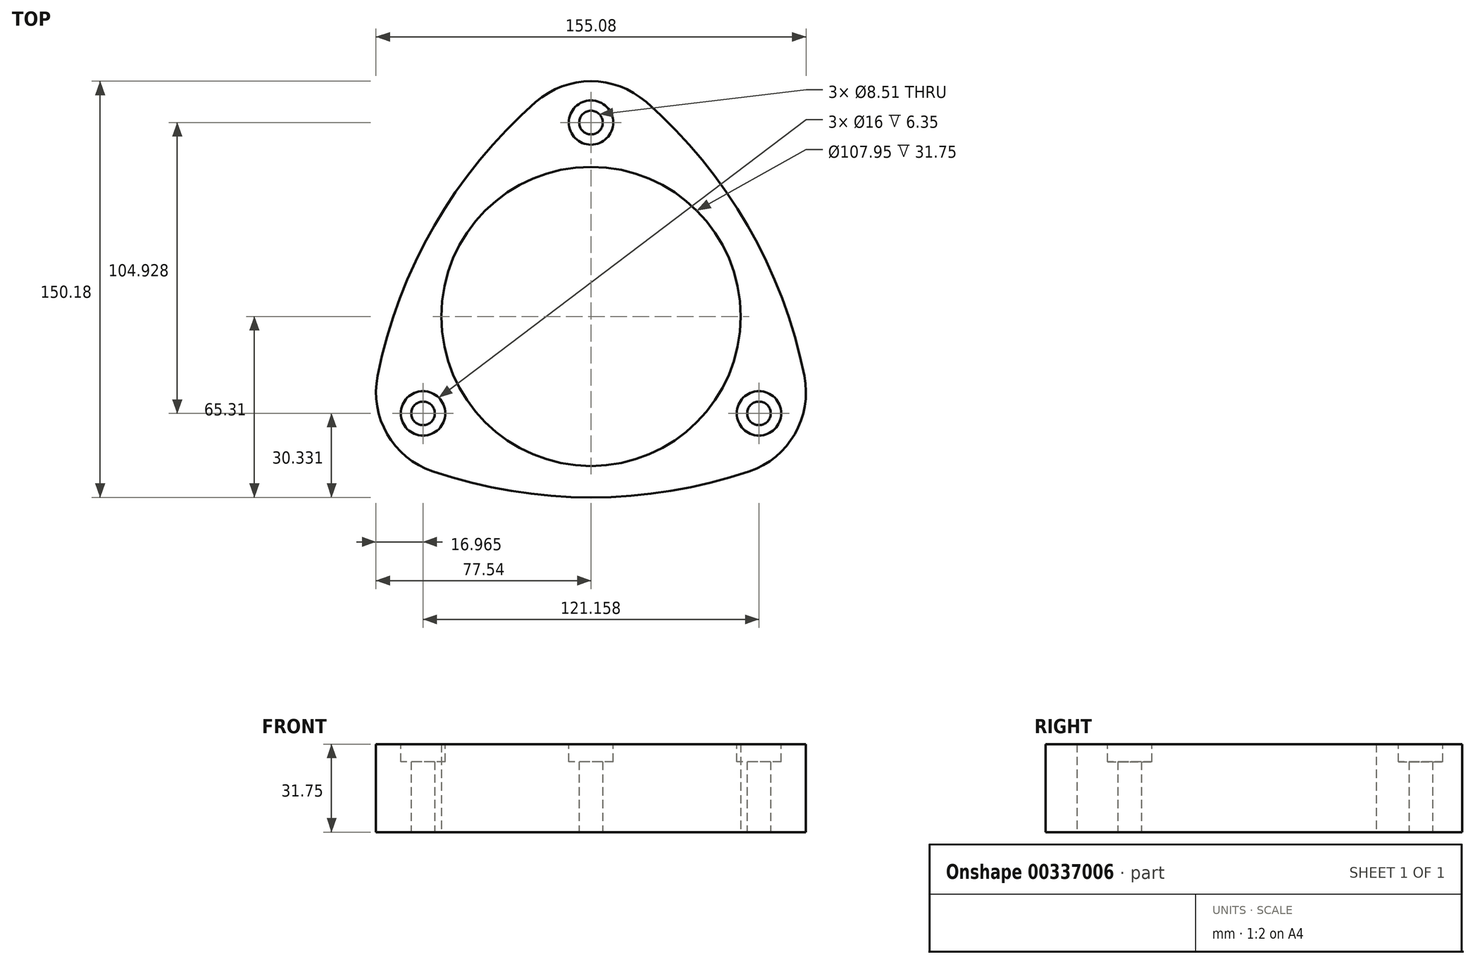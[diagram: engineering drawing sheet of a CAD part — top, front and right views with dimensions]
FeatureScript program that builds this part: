
annotation { "Feature Type Name" : "Feature", "Feature Type Description" : "" }
export const myFeature = defineFeature(function(context is Context, id is Id, definition is map)
    precondition{}
    {
        {
            var Q0;
            Q0=qCreatedBy(makeId("Top.planeOp"),FACE);
            var sketch = newSketch(context, id + "F0", { "sketchPlane" : qUnion([Q0])});
            skCircle(sketch, "E0", {"center": v(0, 0) * mm, "radius": 53.97 * mm});
            skCircle(sketch, "E1", {"center": v(0, 69.95) * mm, "radius": 4.25 * mm});
            skCircle(sketch, "E2", {"center": v(-60.57, -34.98) * mm, "radius": 4.25 * mm});
            skCircle(sketch, "E3", {"center": v(60.58, -34.97) * mm, "radius": 4.25 * mm});
            skArc(sketch, "E4", {"start": v(19.92, 77.36) * mm, "mid": v(0, 84.87) * mm, "end": v(-19.92, 77.36) * mm});
            skLineSegment(sketch, "E5", {"start": v(0, 0) * mm, "end": v(-60.57, -34.98) * mm, "construction": true});
            skLineSegment(sketch, "E6", {"start": v(0, 0) * mm, "end": v(60.58, -34.97) * mm, "construction": true});
            skLineSegment(sketch, "E7", {"start": v(0, 0) * mm, "end": v(0, 69.95) * mm, "construction": true});
            skArc(sketch, "E8", {"start": v(57.04, -55.92) * mm, "mid": v(73.5, -42.43) * mm, "end": v(76.95, -21.43) * mm});
            skArc(sketch, "E9", {"start": v(-76.95, -21.44) * mm, "mid": v(-73.5, -42.44) * mm, "end": v(-57.03, -55.93) * mm});
            skArc(sketch, "E10", {"start": v(-19.92, 77.36) * mm, "mid": v(-56.56, 32.65) * mm, "end": v(-76.95, -21.44) * mm});
            skArc(sketch, "E11", {"start": v(76.95, -21.43) * mm, "mid": v(56.56, 32.66) * mm, "end": v(19.92, 77.36) * mm});
            skArc(sketch, "E12", {"start": v(-57.03, -55.93) * mm, "mid": v(0, -65.3) * mm, "end": v(57.04, -55.92) * mm});
            skLineSegment(sketch, "E13", {"start": v(-72.91, 84.87) * mm, "end": v(75.56, 84.87) * mm, "construction": true});
            skLineSegment(sketch, "E14", {"start": v(-80.18, -65.3) * mm, "end": v(76.53, -65.3) * mm, "construction": true});
            skLineSegment(sketch, "E15", {"start": v(-12.85, 0) * mm, "end": v(13.55, 0) * mm, "construction": true});
            skSolve(sketch);
        }
        {
            var Q0;
            Q0 = qSketchRegion(id + "F0", true);
            var Q1;
            Q1=makeQuery(id+"F0.imprint","IMPRINT",FACE,{"disambiguationData":[TD([[makeQuery(id+"F0.imprint","IMPRINT",EDGE,{"derivedFrom":sQuery(id+"F0.wireOp",EDGE,"E0")}),-1.0]])]});
            extrude(context, id + "F1", {"entities" : qUnion([Q0, Q1]), "depth" : 31.75 * mm});
        }
        {
            var Q0;
            Q0=makeQuery(id+"F1.opExtrude","CAP_FACE",FACE,{"disambiguationData":[OSD([sQuery(id+"F0.wireOp",EDGE,"E0"),sQuery(id+"F0.wireOp",EDGE,"E1"),sQuery(id+"F0.wireOp",EDGE,"E2"),sQuery(id+"F0.wireOp",EDGE,"E3"),sQuery(id+"F0.wireOp",EDGE,"E4"),sQuery(id+"F0.wireOp",EDGE,"E8"),sQuery(id+"F0.wireOp",EDGE,"E9"),sQuery(id+"F0.wireOp",EDGE,"E10"),sQuery(id+"F0.wireOp",EDGE,"E11"),sQuery(id+"F0.wireOp",EDGE,"E12")])],"isStart":false});
            var sketch = newSketch(context, id + "F2", { "sketchPlane" : qUnion([Q0])});
            skCircle(sketch, "E16", {"center": v(0, 69.95) * mm, "radius": 8 * mm});
            skCircle(sketch, "E17", {"center": v(-60.57, -34.98) * mm, "radius": 8 * mm});
            skCircle(sketch, "E18", {"center": v(60.58, -34.97) * mm, "radius": 8 * mm});
            skSolve(sketch);
        }
        {
            var Q0;
            Q0 = qSketchRegion(id + "F2", true);
            extrude(context, id + "F3", {"entities" : qUnion([Q0]), "operationType" : NewBodyOperationType.REMOVE, "oppositeDirection" : true, "depth" : 6.35 * mm});
        }
    });
